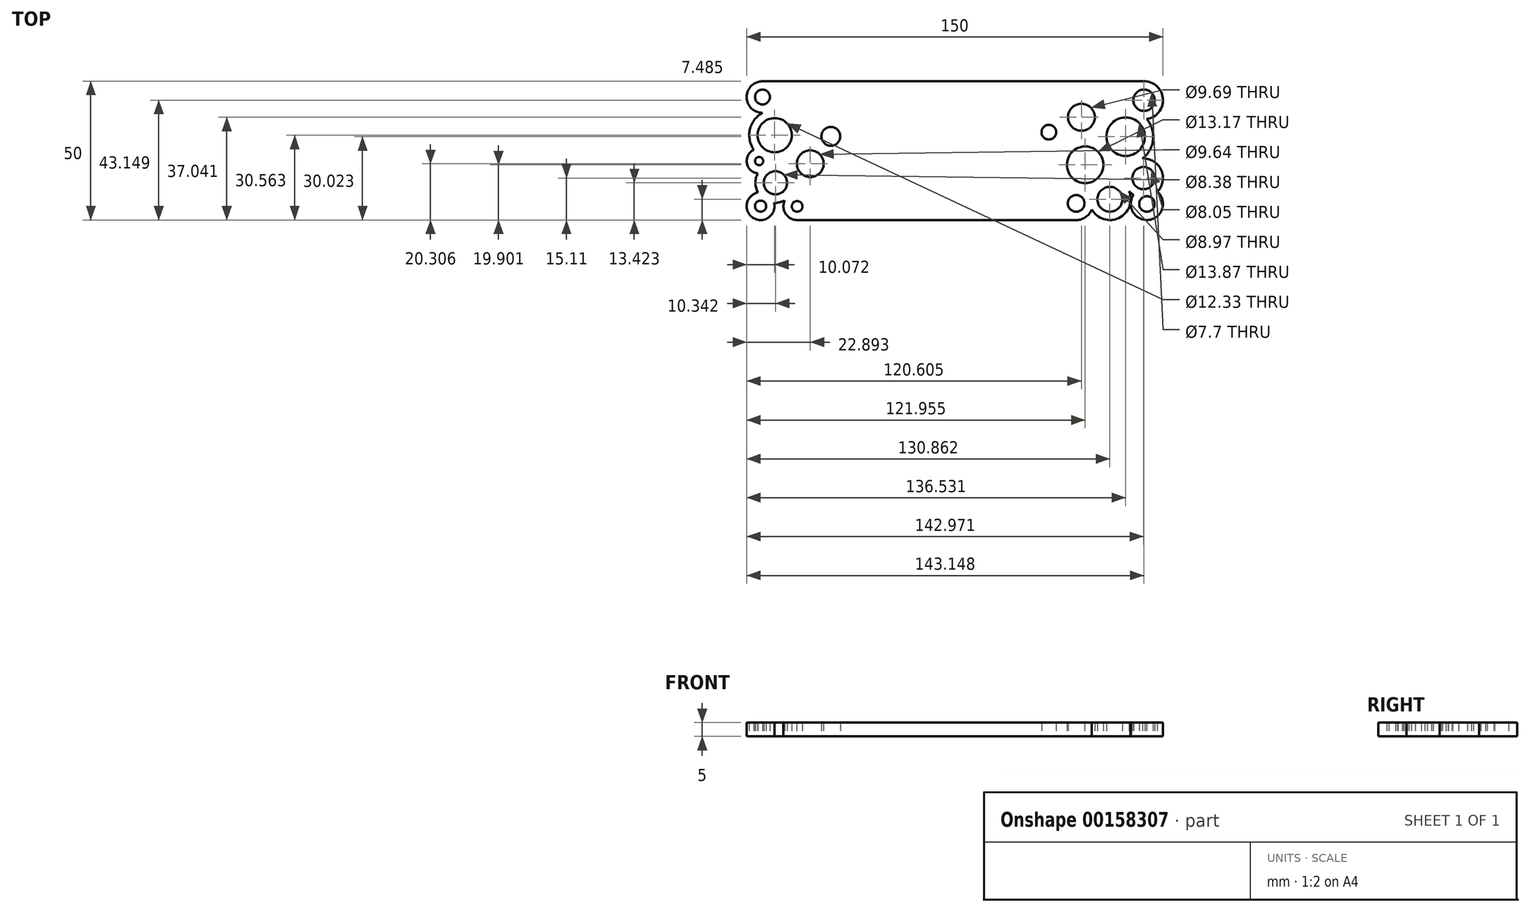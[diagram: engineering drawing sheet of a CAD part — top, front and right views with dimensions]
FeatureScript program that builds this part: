
annotation { "Feature Type Name" : "Feature", "Feature Type Description" : "" }
export const myFeature = defineFeature(function(context is Context, id is Id, definition is map)
    precondition{}
    {
        {
            var Q0;
            Q0=qCreatedBy(makeId("Top.planeOp"),FACE);
            var sketch = newSketch(context, id + "F0", { "sketchPlane" : qUnion([Q0])});
            skCircle(sketch, "E0", {"center": v(-33, 15.45) * mm, "radius": 9.16 * mm});
            skCircle(sketch, "E1", {"center": v(-33, 15.45) * mm, "radius": 6.16 * mm});
            skCircle(sketch, "E2", {"center": v(-37.38, 29.2) * mm, "radius": 2.69 * mm});
            skCircle(sketch, "E3", {"center": v(-37.38, 29.2) * mm, "radius": 5.69 * mm});
            skCircle(sketch, "E4", {"center": v(100.08, 28.04) * mm, "radius": 6.85 * mm});
            skCircle(sketch, "E5", {"center": v(100.08, 28.04) * mm, "radius": 3.85 * mm});
            skCircle(sketch, "E6", {"center": v(75.65, -9.1) * mm, "radius": 6 * mm});
            skCircle(sketch, "E7", {"center": v(75.65, -9.1) * mm, "radius": 3 * mm});
            skCircle(sketch, "E8", {"center": v(-38.06, -10.1) * mm, "radius": 5 * mm});
            skCircle(sketch, "E9", {"center": v(-38.06, -10.1) * mm, "radius": 2 * mm});
            skLineSegment(sketch, "E10", {"start": v(-37.38, 34.89) * mm, "end": v(100.08, 34.89) * mm});
            skCircle(sketch, "E11", {"center": v(93.46, 14.91) * mm, "radius": 9.93 * mm});
            skCircle(sketch, "E12", {"center": v(93.46, 14.91) * mm, "radius": 6.93 * mm});
            skCircle(sketch, "E13", {"center": v(-24.9, -10.19) * mm, "radius": 4.92 * mm});
            skCircle(sketch, "E14", {"center": v(-24.9, -10.19) * mm, "radius": 1.92 * mm});
            skLineSegment(sketch, "E15", {"start": v(-24.9, -15.11) * mm, "end": v(75.65, -15.11) * mm});
            skCircle(sketch, "E16", {"center": v(-38.6, 6.14) * mm, "radius": 4.48 * mm});
            skCircle(sketch, "E17", {"center": v(-38.6, 6.14) * mm, "radius": 1.48 * mm});
            skCircle(sketch, "E18", {"center": v(-32.73, -1.69) * mm, "radius": 7.2 * mm});
            skCircle(sketch, "E19", {"center": v(-32.73, -1.69) * mm, "radius": 4.2 * mm});
            skCircle(sketch, "E20", {"center": v(-20.18, 5.2) * mm, "radius": 4.82 * mm});
            skCircle(sketch, "E21", {"center": v(-12.75, 15.05) * mm, "radius": 3.4 * mm});
            skCircle(sketch, "E22", {"center": v(78.88, 4.8) * mm, "radius": 6.59 * mm});
            skCircle(sketch, "E23", {"center": v(77.54, 21.93) * mm, "radius": 4.85 * mm});
            skCircle(sketch, "E24", {"center": v(65.8, 16.53) * mm, "radius": 2.64 * mm});
            skCircle(sketch, "E25", {"center": v(99.9, 0) * mm, "radius": 7.03 * mm});
            skCircle(sketch, "E26", {"center": v(99.9, 0) * mm, "radius": 4.03 * mm});
            skCircle(sketch, "E27", {"center": v(101.13, -9.31) * mm, "radius": 5.8 * mm});
            skCircle(sketch, "E28", {"center": v(101.13, -9.31) * mm, "radius": 2.8 * mm});
            skCircle(sketch, "E29", {"center": v(87.8, -7.63) * mm, "radius": 7.49 * mm});
            skCircle(sketch, "E30", {"center": v(87.8, -7.63) * mm, "radius": 4.49 * mm});
            skSolve(sketch);
        }
        {
            var Q0;
            Q0 = qSketchRegion(id + "F0", true);
            extrude(context, id + "F1", {"entities" : qUnion([Q0]), "depth" : 5 * mm});
        }
    });
